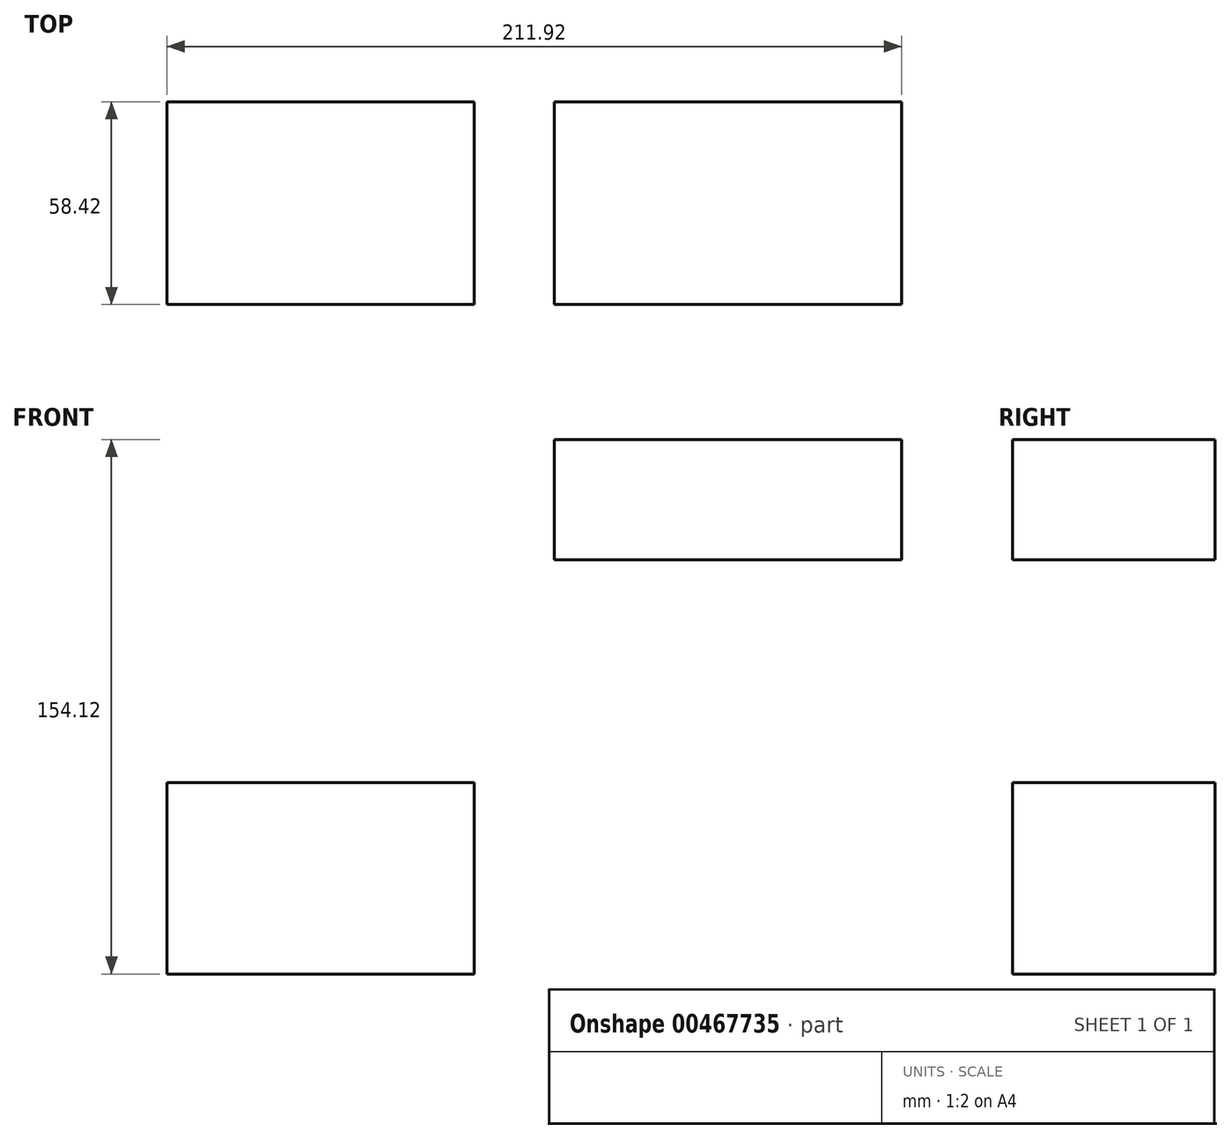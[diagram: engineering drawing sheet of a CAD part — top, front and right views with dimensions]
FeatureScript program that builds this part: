
annotation { "Feature Type Name" : "Feature", "Feature Type Description" : "" }
export const myFeature = defineFeature(function(context is Context, id is Id, definition is map)
    precondition{}
    {
        {
            var Q0;
            Q0=qCreatedBy(makeId("Front.planeOp"),FACE);
            var sketch = newSketch(context, id + "F0", { "sketchPlane" : qUnion([Q0])});
            skLineSegment(sketch, "E0.bottom", {"start": v(-32.1, -27.61) * mm, "end": v(-120.73, -27.61) * mm});
            skLineSegment(sketch, "E0.top", {"start": v(-32.1, 27.61) * mm, "end": v(-120.73, 27.61) * mm});
            skLineSegment(sketch, "E0.left", {"start": v(-32.1, -27.61) * mm, "end": v(-32.1, 27.61) * mm});
            skLineSegment(sketch, "E0.right", {"start": v(-120.73, -27.61) * mm, "end": v(-120.73, 27.61) * mm});
            skPoint(sketch, "E0.middle", {"position": v(-76.42, 0) * mm});
            skLineSegment(sketch, "E1.bottom", {"start": v(91.19, 91.83) * mm, "end": v(-9, 91.83) * mm});
            skLineSegment(sketch, "E1.top", {"start": v(91.19, 126.5) * mm, "end": v(-9, 126.5) * mm});
            skLineSegment(sketch, "E1.left", {"start": v(91.19, 91.83) * mm, "end": v(91.19, 126.5) * mm});
            skLineSegment(sketch, "E1.right", {"start": v(-9, 91.83) * mm, "end": v(-9, 126.5) * mm});
            skPoint(sketch, "E1.middle", {"position": v(41.1, 109.17) * mm});
            skLineSegment(sketch, "E2", {"start": v(-32.1, 54.58) * mm, "end": v(-32.1, 27.61) * mm});
            skArc(sketch, "E3", {"start": v(-32.1, 54.58) * mm, "mid": v(-16.9, 93.2) * mm, "end": v(20.55, 111.1) * mm});
            skFitSpline(sketch, "E4", {"points": [v(-57.15, 102.1) * mm, v(-120.73, 27.61) * mm], "startDerivative": vector(-10.74, -49.03) * mm, "endDerivative": vector(-10.74, -49.03) * mm});
            skSolve(sketch);
        }
        {
            var Q0;
            Q0 = qSketchRegion(id + "F0", true);
            extrude(context, id + "F1", {"entities" : qUnion([Q0]), "depth" : 58.42 * mm});
        }
    });
